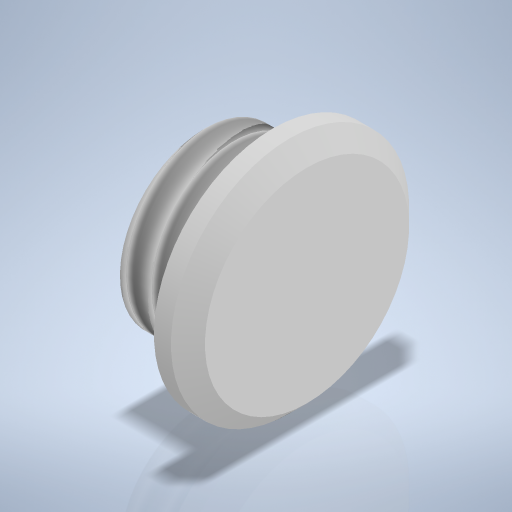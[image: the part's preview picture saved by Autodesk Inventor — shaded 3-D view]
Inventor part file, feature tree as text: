
AUTODESK INVENTOR PART (.ipt)
format: ipt  version: 2024 (Build 280153000, 153)  size: 256,512 bytes
history: native  units: mm
features: revolve x1, chamfer x1, thread x1, sketch x1
ambient origin geometry x8: Origin, YZ Plane, XZ Plane, XY Plane, X Axis, Y Axis, Z Axis, Center Point
bodies: Volumenkörper1 (feature_tree)
feature tree (4):
  revolve  "Umdrehung1"
  chamfer  "Fasen1"  Distance=10.0mm
  thread  "Gewinde1"  [1 undecoded]
  sketch  "Skizze1"  dims[d0=14.0mm d1=10.0mm d2=2.0mm d3=4.0mm d4=90.0deg d5=1.0mm d6=2.0mm d7=45.0deg d8=4.0mm d9=0.0mm]
note: 1 required parameter value undecoded (feature->parameter linkage not recoverable at this tier; creation-order binding heuristic only, values carry confidence <= 0.55)
